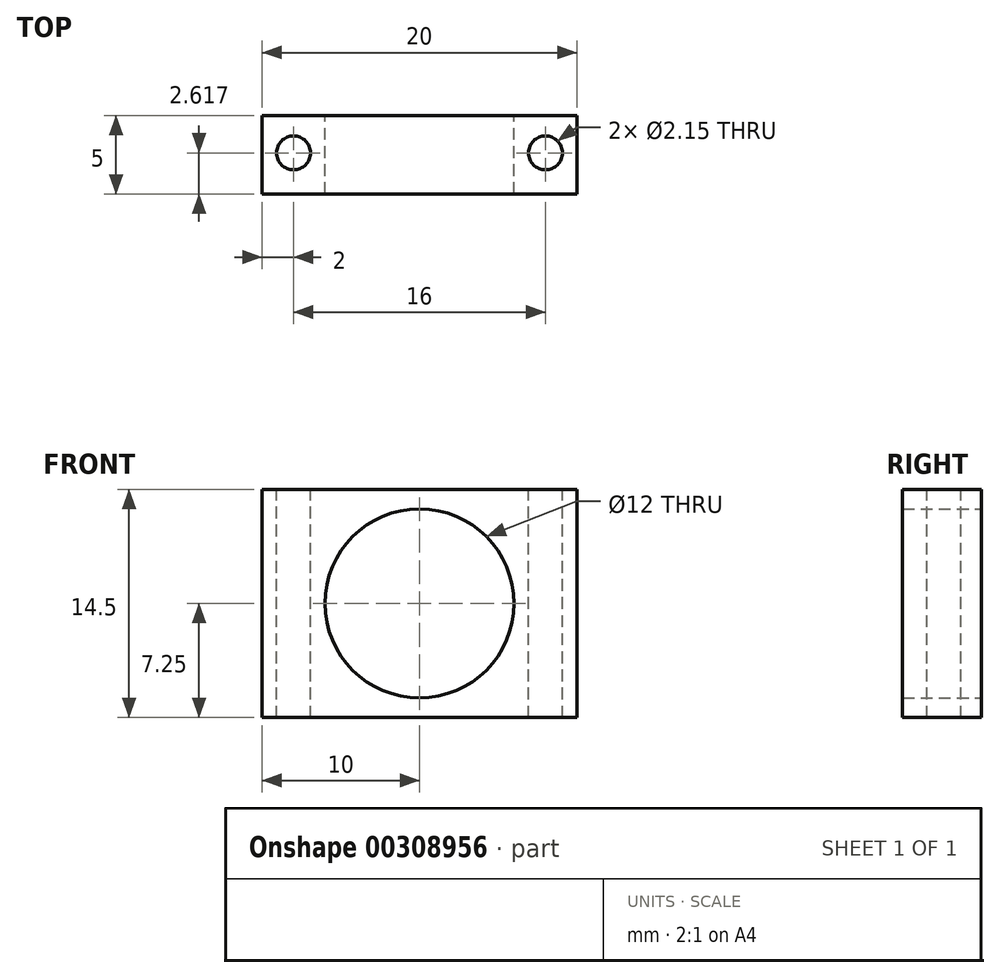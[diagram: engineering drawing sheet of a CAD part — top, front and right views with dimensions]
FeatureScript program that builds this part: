
annotation { "Feature Type Name" : "Feature", "Feature Type Description" : "" }
export const myFeature = defineFeature(function(context is Context, id is Id, definition is map)
    precondition{}
    {
        {
            var Q0;
            Q0=qCreatedBy(makeId("Front.planeOp"),FACE);
            var sketch = newSketch(context, id + "F0", { "sketchPlane" : qUnion([Q0])});
            skLineSegment(sketch, "E0.bottom", {"start": v(-10, 7.25) * mm, "end": v(10, 7.25) * mm});
            skLineSegment(sketch, "E0.top", {"start": v(-10, -7.25) * mm, "end": v(10, -7.25) * mm});
            skLineSegment(sketch, "E0.left", {"start": v(-10, 7.25) * mm, "end": v(-10, -7.25) * mm});
            skLineSegment(sketch, "E0.right", {"start": v(10, 7.25) * mm, "end": v(10, -7.25) * mm});
            skCircle(sketch, "E1", {"center": v(0, 0) * mm, "radius": 6 * mm});
            skSolve(sketch);
        }
        {
            var Q0;
            Q0=makeQuery(id+"F0.imprint","IMPRINT",FACE,{"disambiguationData":[TD([[makeQuery(id+"F0.imprint","IMPRINT",EDGE,{"derivedFrom":sQuery(id+"F0.wireOp",EDGE,"E0.bottom")}),-1.0]])]});
            extrude(context, id + "F1", {"entities" : qUnion([Q0]), "depth" : 5 * mm});
        }
        {
            var Q0;
            Q0=makeQuery(id+"F1.opExtrude","SWEPT_FACE",FACE,{"disambiguationData":[OSD([sQuery(id+"F0.wireOp",EDGE,"E0.bottom")])]});
            var sketch = newSketch(context, id + "F2", { "sketchPlane" : qUnion([Q0])});
            skLineSegment(sketch, "E2", {"start": v(-8, -2.38) * mm, "end": v(8, -2.38) * mm});
            skSolve(sketch);
        }
        {
            var Q0;
            Q0=sQuery(id+"F2.wireOp",VERTEX,"E2.end");
            var Q1;
            Q1=sQuery(id+"F2.wireOp",VERTEX,"E2.start");
            var Q2;
            Q2=makeQuery(id+"F1.opExtrude","SWEPT_BODY",BODY,{"disambiguationData":[OSD([sQuery(id+"F0.wireOp",EDGE,"E0.bottom"),sQuery(id+"F0.wireOp",EDGE,"E0.top"),sQuery(id+"F0.wireOp",EDGE,"E0.left"),sQuery(id+"F0.wireOp",EDGE,"E0.right"),sQuery(id+"F0.wireOp",EDGE,"E1")])]});
            hole(context, id + "F3", {"style" : HoleStyle.SIMPLE, "endStyle" : HoleEndStyle.THROUGH, "standardTappedOrClearance" : lookupTablePath({ "standard" : "ISO", "engagement" : "75%", "pitch" : "0.35 mm", "size" : "M2.5", "type" : "Tapped" }), "standardBlindInLast" : lookupTablePath({ "standard" : "ISO", "fit" : "Normal", "engagement" : "75%", "pitch" : "0.35 mm", "size" : "M2.5", "type" : "Clearance & tapped" }), "holeDiameter" : 2.15 * mm, "majorDiameter" : 2.5 * mm, "showTappedDepth" : true, "tappedDepth" : 12 * mm, "tapClearance" : 3, "locations" : qUnion([Q0, Q1]), "scope" : qUnion([Q2])});
        }
    });
